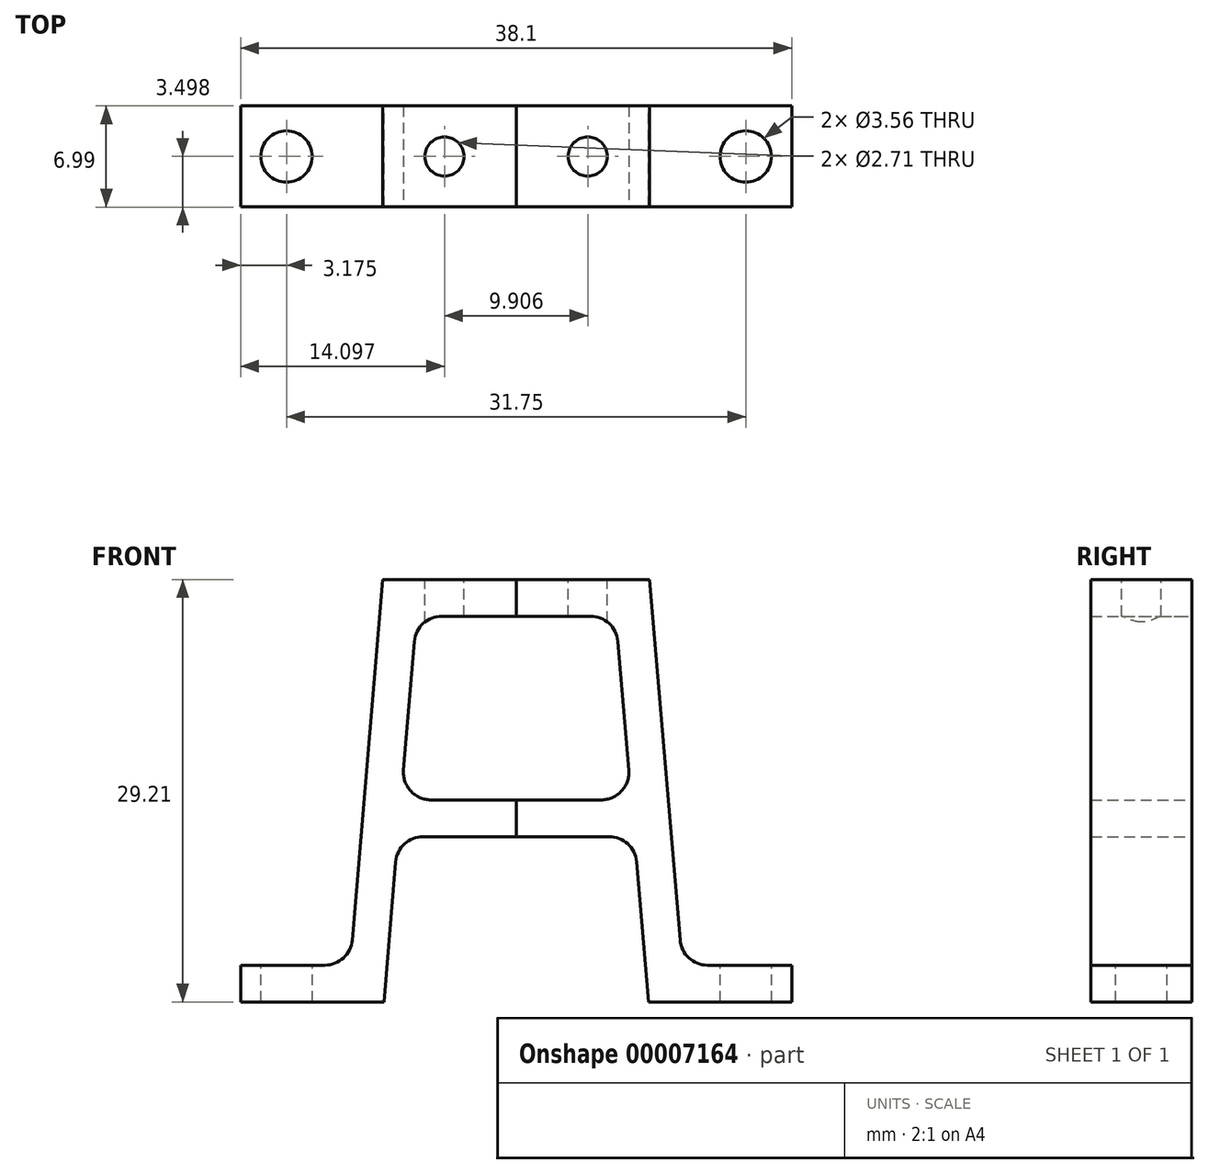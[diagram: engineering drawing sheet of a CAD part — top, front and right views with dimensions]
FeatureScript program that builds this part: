
annotation { "Feature Type Name" : "Feature", "Feature Type Description" : "" }
export const myFeature = defineFeature(function(context is Context, id is Id, definition is map)
    precondition{}
    {
        {
            var Q0;
            Q0=qCreatedBy(makeId("Front.planeOp"),FACE);
            var sketch = newSketch(context, id + "F0", { "sketchPlane" : qUnion([Q0])});
            skLineSegment(sketch, "E0", {"start": v(0, 29.2) * mm, "end": v(9.22, 29.2) * mm});
            skLineSegment(sketch, "E1", {"start": v(9.22, 29.21) * mm, "end": v(11.48, 2.54) * mm});
            skLineSegment(sketch, "E2", {"start": v(11.48, 2.54) * mm, "end": v(19.05, 2.54) * mm});
            skLineSegment(sketch, "E3", {"start": v(19.05, 2.54) * mm, "end": v(19.05, 0) * mm});
            skLineSegment(sketch, "E4", {"start": v(19.05, 0) * mm, "end": v(9.14, 0) * mm});
            skLineSegment(sketch, "E5", {"start": v(9.14, 0) * mm, "end": v(8.18, 11.43) * mm});
            skLineSegment(sketch, "E6", {"start": v(8.18, 11.43) * mm, "end": v(0, 11.43) * mm});
            skLineSegment(sketch, "E7", {"start": v(0, 11.43) * mm, "end": v(0, 13.97) * mm});
            skLineSegment(sketch, "E8", {"start": v(0, 13.97) * mm, "end": v(7.96, 13.97) * mm});
            skLineSegment(sketch, "E9", {"start": v(7.96, 13.97) * mm, "end": v(6.89, 26.67) * mm});
            skLineSegment(sketch, "E10", {"start": v(6.89, 26.67) * mm, "end": v(0, 26.67) * mm});
            skLineSegment(sketch, "E11", {"start": v(0, 26.67) * mm, "end": v(0, 29.2) * mm});
            skPoint(sketch, "E12", {"position": v(0, 12.7) * mm});
            skLineSegment(sketch, "E13", {"start": v(7.42, 20.32) * mm, "end": v(9.95, 20.53) * mm});
            skSolve(sketch);
        }
        {
            var Q0;
            Q0 = qSketchRegion(id + "F0", true);
            extrude(context, id + "F1", {"entities" : qUnion([Q0]), "depth" : 7 * mm});
        }
        {
            var Q0;
            Q0=makeQuery(id+"F1.opExtrude","SWEPT_EDGE",EDGE,{"disambiguationData":[OSD([sQuery(id+"F0.wireOp",EDGE,"E1"),sQuery(id+"F0.wireOp",EDGE,"E2")])]});
            var Q1;
            Q1=makeQuery(id+"F1.opExtrude","SWEPT_EDGE",EDGE,{"disambiguationData":[OSD([sQuery(id+"F0.wireOp",EDGE,"E5"),sQuery(id+"F0.wireOp",EDGE,"E6")])]});
            var Q2;
            Q2=makeQuery(id+"F1.opExtrude","SWEPT_EDGE",EDGE,{"disambiguationData":[OSD([sQuery(id+"F0.wireOp",EDGE,"E9"),sQuery(id+"F0.wireOp",EDGE,"E10")])]});
            var Q3;
            Q3=makeQuery(id+"F1.opExtrude","SWEPT_EDGE",EDGE,{"disambiguationData":[OSD([sQuery(id+"F0.wireOp",EDGE,"E8"),sQuery(id+"F0.wireOp",EDGE,"E9")])]});
            fillet(context, id + "F2", {"entities" : qUnion([Q0, Q1, Q2, Q3]), "radius" : 1.9 * mm, "tangentPropagation" : true, "allowEdgeOverflow" : false});
        }
        {
            var Q0;
            Q0=makeQuery(id+"F1.opExtrude","SWEPT_FACE",FACE,{"disambiguationData":[OSD([sQuery(id+"F0.wireOp",EDGE,"E2")])]});
            var sketch = newSketch(context, id + "F3", { "sketchPlane" : qUnion([Q0])});
            skCircle(sketch, "E14", {"center": v(15.88, -3.5) * mm, "radius": 1.78 * mm});
            skPoint(sketch, "E15", {"position": v(19.05, -3.5) * mm});
            skSolve(sketch);
        }
        {
            var Q0;
            Q0 = qSketchRegion(id + "F3", true);
            extrude(context, id + "F4", {"entities" : qUnion([Q0]), "operationType" : NewBodyOperationType.REMOVE, "endBound" : BoundingType.UP_TO_NEXT, "oppositeDirection" : true, "depth" : 25.4 * mm});
        }
        {
            var Q0;
            Q0=makeQuery(id+"F1.opExtrude","SWEPT_FACE",FACE,{"disambiguationData":[OSD([sQuery(id+"F0.wireOp",EDGE,"E0")])]});
            var sketch = newSketch(context, id + "F5", { "sketchPlane" : qUnion([Q0])});
            skCircle(sketch, "E16", {"center": v(4.95, -3.5) * mm, "radius": 1.35 * mm});
            skPoint(sketch, "E17", {"position": v(9.22, -3.5) * mm});
            skSolve(sketch);
        }
        {
            var Q0;
            Q0 = qSketchRegion(id + "F5", true);
            extrude(context, id + "F6", {"entities" : qUnion([Q0]), "operationType" : NewBodyOperationType.REMOVE, "endBound" : BoundingType.UP_TO_NEXT, "oppositeDirection" : true, "depth" : 25.4 * mm});
        }
        {
            var Q0;
            Q0=makeQuery(id+"F1.opExtrude","SWEPT_BODY",BODY,{"disambiguationData":[OSD([sQuery(id+"F0.wireOp",EDGE,"E0"),sQuery(id+"F0.wireOp",EDGE,"E1"),sQuery(id+"F0.wireOp",EDGE,"E2"),sQuery(id+"F0.wireOp",EDGE,"E3"),sQuery(id+"F0.wireOp",EDGE,"E4"),sQuery(id+"F0.wireOp",EDGE,"E5"),sQuery(id+"F0.wireOp",EDGE,"E6"),sQuery(id+"F0.wireOp",EDGE,"E7"),sQuery(id+"F0.wireOp",EDGE,"E8"),sQuery(id+"F0.wireOp",EDGE,"E9"),sQuery(id+"F0.wireOp",EDGE,"E10"),sQuery(id+"F0.wireOp",EDGE,"E11")])]});
            var Q1;
            Q1=qCreatedBy(makeId("Right.planeOp"),FACE);
            mirror(context, id + "F7", {"entities" : qUnion([Q0]), "mirrorPlane" : qUnion([Q1])});
        }
    });
